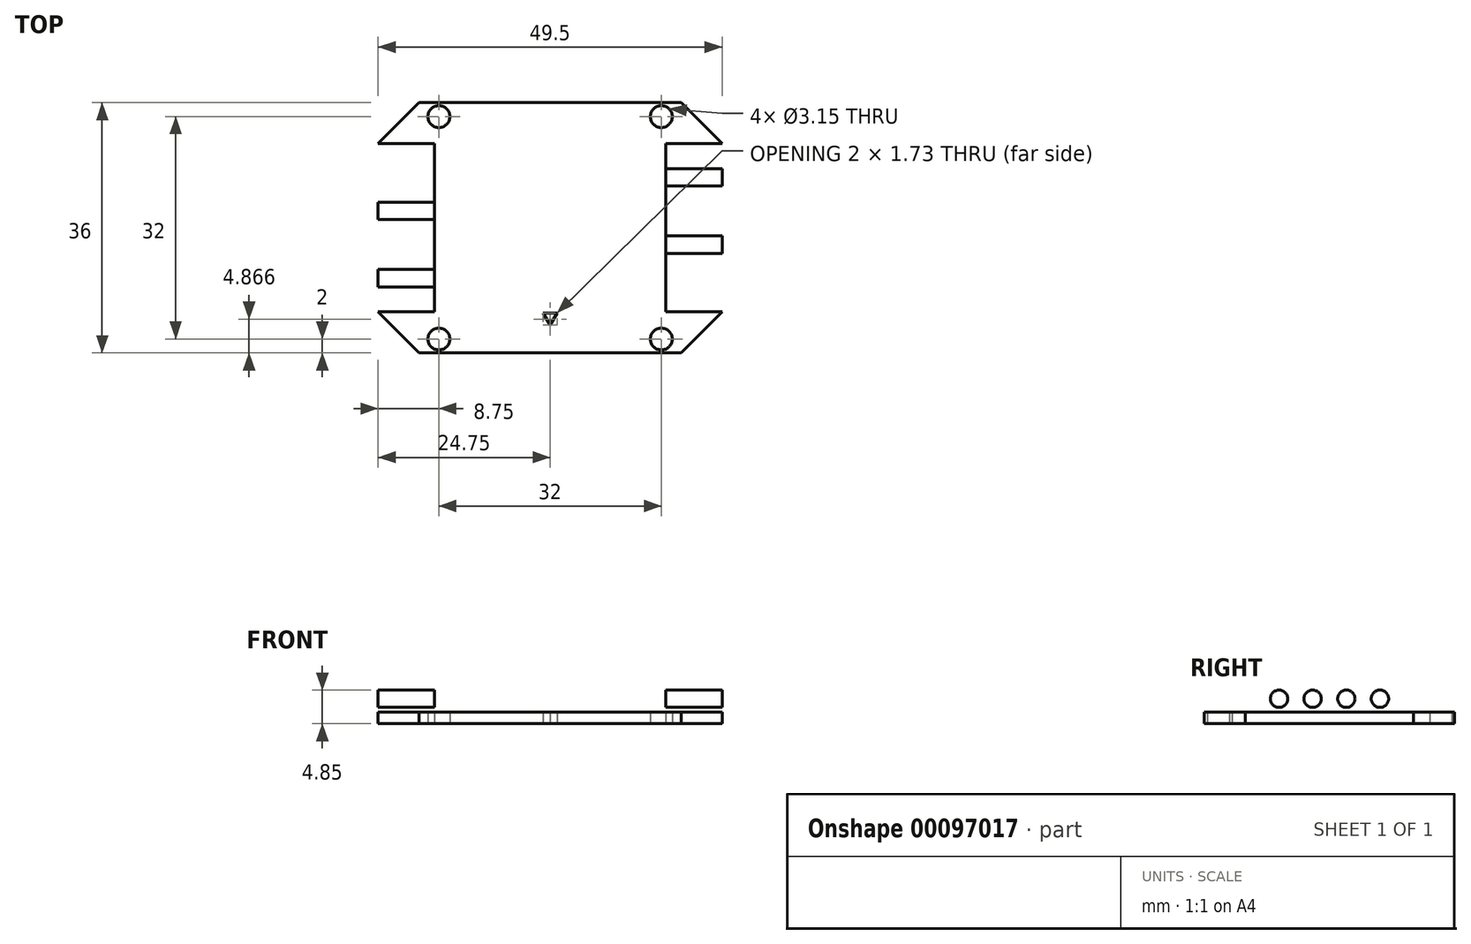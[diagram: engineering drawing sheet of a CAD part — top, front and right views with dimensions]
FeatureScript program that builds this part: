
annotation { "Feature Type Name" : "Feature", "Feature Type Description" : "" }
export const myFeature = defineFeature(function(context is Context, id is Id, definition is map)
    precondition{}
    {
        {
            var Q0;
            Q0=qCreatedBy(makeId("Top.planeOp"),FACE);
            var sketch = newSketch(context, id + "F0", { "sketchPlane" : qUnion([Q0])});
            skPoint(sketch, "E0.middle", {"position": v(0, 0) * mm});
            skCircle(sketch, "E1", {"center": v(-16, 16) * mm, "radius": 1.57 * mm});
            skCircle(sketch, "E2", {"center": v(16, 16) * mm, "radius": 1.57 * mm});
            skCircle(sketch, "E3", {"center": v(-16, -16) * mm, "radius": 1.57 * mm});
            skCircle(sketch, "E4", {"center": v(16, -16) * mm, "radius": 1.57 * mm});
            skLineSegment(sketch, "E5.bottom", {"start": v(-18.85, 18) * mm, "end": v(18.85, 18) * mm});
            skLineSegment(sketch, "E5.top", {"start": v(-18.85, -18) * mm, "end": v(18.85, -18) * mm});
            skLineSegment(sketch, "E5.left", {"start": v(-24.75, 12.1) * mm, "end": v(-24.75, -12.1) * mm});
            skLineSegment(sketch, "E5.right", {"start": v(24.75, 12.1) * mm, "end": v(24.75, -12.1) * mm});
            skLineSegment(sketch, "E6", {"start": v(24.75, 12.1) * mm, "end": v(18.85, 18) * mm});
            skLineSegment(sketch, "E7", {"start": v(24.75, -12.1) * mm, "end": v(18.85, -18) * mm});
            skLineSegment(sketch, "E8", {"start": v(-18.85, -18) * mm, "end": v(-24.75, -12.1) * mm});
            skLineSegment(sketch, "E9", {"start": v(-18.85, 18) * mm, "end": v(-24.75, 12.1) * mm});
            skLineSegment(sketch, "E10", {"start": v(0, -14) * mm, "end": v(1, -12.27) * mm});
            skLineSegment(sketch, "E11", {"start": v(1, -12.27) * mm, "end": v(-1, -12.27) * mm});
            skLineSegment(sketch, "E12", {"start": v(-1, -12.27) * mm, "end": v(0, -14) * mm});
            skLineSegment(sketch, "E13", {"start": v(-16, -16) * mm, "end": v(-16, -18) * mm});
            skLineSegment(sketch, "E14", {"start": v(16, -16) * mm, "end": v(16, -18) * mm});
            skLineSegment(sketch, "E15", {"start": v(-16, 16) * mm, "end": v(-16, 18) * mm});
            skLineSegment(sketch, "E16", {"start": v(16, 16) * mm, "end": v(16, 18) * mm});
            skLineSegment(sketch, "E17", {"start": v(-16, 16) * mm, "end": v(-20.85, 16) * mm});
            skLineSegment(sketch, "E18", {"start": v(16, 16) * mm, "end": v(20.85, 16) * mm});
            skLineSegment(sketch, "E19", {"start": v(16, -16) * mm, "end": v(20.85, -16) * mm});
            skLineSegment(sketch, "E20", {"start": v(-16, -16) * mm, "end": v(-20.85, -16) * mm});
            skSolve(sketch);
        }
        {
            var Q0;
            Q0=makeQuery(id+"F0.imprint","IMPRINT",FACE,{"disambiguationData":[TD([[makeQuery(id+"F0.imprint","IMPRINT",EDGE,{"derivedFrom":sQuery(id+"F0.wireOp",EDGE,"E1")}),-1.0]])]});
            var Q1;
            {var subQ30=sQuery(id+"F0.wireOp",EDGE,"E5.left");Q1=makeQuery(id+"F0.imprint","IMPRINT",FACE,{"disambiguationData":[TD([[makeQuery(id+"F0.imprint","IMPRINT",EDGE,{"derivedFrom":subQ30}),1.0]])]});}
            var Q2;
            {var subQ0=sQuery(id+"F0.wireOp",EDGE,"E16");var subQ3=sQuery(id+"F0.wireOp",EDGE,"E2");var subQ4=makeQuery(id+"F0.imprint","INTERSECT",VERTEX,{"derivedFrom":[subQ3,subQ0]});Q2=makeQuery(id+"F0.imprint","IMPRINT",FACE,{"disambiguationData":[TD([[makeQuery(id+"F0.imprint","IMPRINT",EDGE,{"disambiguationData":[TD([[subQ4,1.0]])],"derivedFrom":subQ3}),-1.0]])]});}
            var Q3;
            {var subQ0=sQuery(id+"F0.wireOp",EDGE,"E14");var subQ3=sQuery(id+"F0.wireOp",EDGE,"E4");var subQ4=makeQuery(id+"F0.imprint","INTERSECT",VERTEX,{"derivedFrom":[subQ3,subQ0]});Q3=makeQuery(id+"F0.imprint","IMPRINT",FACE,{"disambiguationData":[TD([[makeQuery(id+"F0.imprint","IMPRINT",EDGE,{"disambiguationData":[TD([[subQ4,-1.0]])],"derivedFrom":subQ3}),-1.0]])]});}
            var Q4;
            {var subQ0=sQuery(id+"F0.wireOp",EDGE,"E13");var subQ3=sQuery(id+"F0.wireOp",EDGE,"E3");var subQ4=makeQuery(id+"F0.imprint","INTERSECT",VERTEX,{"derivedFrom":[subQ3,subQ0]});Q4=makeQuery(id+"F0.imprint","IMPRINT",FACE,{"disambiguationData":[TD([[makeQuery(id+"F0.imprint","IMPRINT",EDGE,{"disambiguationData":[TD([[subQ4,1.0]])],"derivedFrom":subQ3}),-1.0]])]});}
            extrude(context, id + "F1", {"entities" : qUnion([Q0, Q1, Q2, Q3, Q4]), "depth" : 1.7 * mm});
        }
        {
            var Q0;
            Q0=makeQuery(id+"F1.opExtrude","CAP_FACE",FACE,{"disambiguationData":[OSD([sQuery(id+"F0.wireOp",EDGE,"E1"),sQuery(id+"F0.wireOp",EDGE,"E2"),sQuery(id+"F0.wireOp",EDGE,"E3"),sQuery(id+"F0.wireOp",EDGE,"E4"),sQuery(id+"F0.wireOp",EDGE,"E5.bottom"),sQuery(id+"F0.wireOp",EDGE,"E5.top"),sQuery(id+"F0.wireOp",EDGE,"E5.left"),sQuery(id+"F0.wireOp",EDGE,"E5.right"),sQuery(id+"F0.wireOp",EDGE,"E6"),sQuery(id+"F0.wireOp",EDGE,"E7"),sQuery(id+"F0.wireOp",EDGE,"E8"),sQuery(id+"F0.wireOp",EDGE,"E9")])],"isStart":false});
            var sketch = newSketch(context, id + "F2", { "sketchPlane" : qUnion([Q0])});
            skLineSegment(sketch, "E21.bottom", {"start": v(-24.75, 12.1) * mm, "end": v(-16.65, 12.1) * mm});
            skLineSegment(sketch, "E21.top", {"start": v(-24.75, -12.1) * mm, "end": v(-16.65, -12.1) * mm});
            skLineSegment(sketch, "E21.left", {"start": v(-24.75, 12.1) * mm, "end": v(-24.75, -12.1) * mm});
            skLineSegment(sketch, "E21.right", {"start": v(-16.65, 12.1) * mm, "end": v(-16.65, -12.1) * mm});
            skLineSegment(sketch, "E22.bottom", {"start": v(24.75, 12.1) * mm, "end": v(16.65, 12.1) * mm});
            skLineSegment(sketch, "E22.top", {"start": v(24.75, -12.1) * mm, "end": v(16.65, -12.1) * mm});
            skLineSegment(sketch, "E22.left", {"start": v(24.75, 12.1) * mm, "end": v(24.75, -12.1) * mm});
            skLineSegment(sketch, "E22.right", {"start": v(16.65, 12.1) * mm, "end": v(16.65, -12.1) * mm});
            skSolve(sketch);
        }
        {
            var Q0;
            Q0=makeQuery(id+"F2.imprint","IMPRINT",FACE,{"disambiguationData":[TD([[makeQuery(id+"F2.imprint","IMPRINT",EDGE,{"derivedFrom":sQuery(id+"F2.wireOp",EDGE,"E21.bottom")}),-1.0]])]});
            var Q1;
            Q1=makeQuery(id+"F2.imprint","IMPRINT",FACE,{"disambiguationData":[TD([[makeQuery(id+"F2.imprint","IMPRINT",EDGE,{"derivedFrom":sQuery(id+"F2.wireOp",EDGE,"E22.bottom")}),1.0]])]});
            extrude(context, id + "F3", {"entities" : qUnion([Q0, Q1]), "operationType" : NewBodyOperationType.ADD, "depth" : 5.5 * mm});
        }
        {
            var Q0;
            Q0=makeQuery(id+"F3.boolean.opBoolean","MERGE",FACE,{"derivedFrom":[makeQuery(id+"F1.opExtrude","SWEPT_FACE",FACE,{"disambiguationData":[OSD([sQuery(id+"F0.wireOp",EDGE,"E5.left")])]}),makeQuery(id+"F3.opExtrude","SWEPT_FACE",FACE,{"disambiguationData":[OSD([sQuery(id+"F2.wireOp",EDGE,"E21.left")])]})]});
            var sketch = newSketch(context, id + "F4", { "sketchPlane" : qUnion([Q0])});
            skPoint(sketch, "E23", {"position": v(-12.1, 3.6) * mm});
            skPoint(sketch, "E24", {"position": v(12.1, 3.6) * mm});
            skLineSegment(sketch, "E25", {"start": v(-12.1, 3.6) * mm, "end": v(12.1, 3.6) * mm});
            skPoint(sketch, "E26", {"position": v(-7.26, 3.6) * mm});
            skPoint(sketch, "E27", {"position": v(-2.42, 3.6) * mm});
            skPoint(sketch, "E28", {"position": v(2.42, 3.6) * mm});
            skPoint(sketch, "E29", {"position": v(12.08, 3.6) * mm});
            skPoint(sketch, "E30", {"position": v(7.26, 3.6) * mm});
            skCircle(sketch, "E31", {"center": v(-7.26, 3.6) * mm, "radius": 1.25 * mm});
            skCircle(sketch, "E32", {"center": v(-2.42, 3.6) * mm, "radius": 1.25 * mm});
            skCircle(sketch, "E33", {"center": v(2.42, 3.6) * mm, "radius": 1.25 * mm});
            skCircle(sketch, "E34", {"center": v(7.26, 3.6) * mm, "radius": 1.25 * mm});
            skSolve(sketch);
        }
        {
            var Q0;
            Q0=makeQuery(id+"F3.boolean.opBoolean","MERGE",FACE,{"derivedFrom":[makeQuery(id+"F1.opExtrude","SWEPT_FACE",FACE,{"disambiguationData":[OSD([sQuery(id+"F0.wireOp",EDGE,"E5.right")])]}),makeQuery(id+"F3.opExtrude","SWEPT_FACE",FACE,{"disambiguationData":[OSD([sQuery(id+"F2.wireOp",EDGE,"E22.left")])]})]});
            var sketch = newSketch(context, id + "F5", { "sketchPlane" : qUnion([Q0])});
            skPoint(sketch, "E35", {"position": v(-12.1, 3.6) * mm});
            skPoint(sketch, "E36", {"position": v(12.1, 3.6) * mm});
            skLineSegment(sketch, "E37", {"start": v(-12.1, 3.6) * mm, "end": v(12.1, 3.6) * mm});
            skPoint(sketch, "E38", {"position": v(-7.26, 3.6) * mm});
            skPoint(sketch, "E39", {"position": v(-2.42, 3.6) * mm});
            skPoint(sketch, "E40", {"position": v(2.42, 3.6) * mm});
            skPoint(sketch, "E41", {"position": v(7.26, 3.6) * mm});
            skCircle(sketch, "E42", {"center": v(-7.26, 3.6) * mm, "radius": 1.25 * mm});
            skCircle(sketch, "E43", {"center": v(-2.42, 3.6) * mm, "radius": 1.25 * mm});
            skCircle(sketch, "E44", {"center": v(2.42, 3.6) * mm, "radius": 1.25 * mm});
            skCircle(sketch, "E45", {"center": v(7.26, 3.6) * mm, "radius": 1.25 * mm});
            skSolve(sketch);
        }
        {
            var Q0;
            {var subQ0=sQuery(id+"F5.wireOp",EDGE,"E45");var subQ1=sQuery(id+"F5.wireOp",EDGE,"E37");var subQ2=makeQuery(id+"F5.imprint","INTERSECT",VERTEX,{"disambiguationData":[OD(0.0)],"derivedFrom":[subQ1,subQ0]});Q0=makeQuery(id+"F5.imprint","IMPRINT",FACE,{"disambiguationData":[TD([[makeQuery(id+"F5.imprint","IMPRINT",EDGE,{"disambiguationData":[TD([[subQ2,-1.0]])],"derivedFrom":subQ1}),1.0]])]});}
            var Q1;
            {var subQ0=sQuery(id+"F5.wireOp",EDGE,"E45");var subQ1=sQuery(id+"F5.wireOp",EDGE,"E37");var subQ2=makeQuery(id+"F5.imprint","INTERSECT",VERTEX,{"disambiguationData":[OD(0.0)],"derivedFrom":[subQ1,subQ0]});Q1=makeQuery(id+"F5.imprint","IMPRINT",FACE,{"disambiguationData":[TD([[makeQuery(id+"F5.imprint","IMPRINT",EDGE,{"disambiguationData":[TD([[subQ2,-1.0]])],"derivedFrom":subQ1}),-1.0]])]});}
            var Q2;
            {var subQ0=sQuery(id+"F5.wireOp",EDGE,"E44");var subQ1=sQuery(id+"F5.wireOp",EDGE,"E37");var subQ2=makeQuery(id+"F5.imprint","INTERSECT",VERTEX,{"disambiguationData":[OD(0.0)],"derivedFrom":[subQ1,subQ0]});Q2=makeQuery(id+"F5.imprint","IMPRINT",FACE,{"disambiguationData":[TD([[makeQuery(id+"F5.imprint","IMPRINT",EDGE,{"disambiguationData":[TD([[subQ2,-1.0]])],"derivedFrom":subQ1}),-1.0]])]});}
            var Q3;
            {var subQ0=sQuery(id+"F5.wireOp",EDGE,"E44");var subQ1=sQuery(id+"F5.wireOp",EDGE,"E37");var subQ2=makeQuery(id+"F5.imprint","INTERSECT",VERTEX,{"disambiguationData":[OD(0.0)],"derivedFrom":[subQ1,subQ0]});Q3=makeQuery(id+"F5.imprint","IMPRINT",FACE,{"disambiguationData":[TD([[makeQuery(id+"F5.imprint","IMPRINT",EDGE,{"disambiguationData":[TD([[subQ2,-1.0]])],"derivedFrom":subQ1}),1.0]])]});}
            var Q4;
            {var subQ0=sQuery(id+"F5.wireOp",EDGE,"E43");var subQ1=sQuery(id+"F5.wireOp",EDGE,"E37");var subQ2=makeQuery(id+"F5.imprint","INTERSECT",VERTEX,{"disambiguationData":[OD(0.0)],"derivedFrom":[subQ1,subQ0]});Q4=makeQuery(id+"F5.imprint","IMPRINT",FACE,{"disambiguationData":[TD([[makeQuery(id+"F5.imprint","IMPRINT",EDGE,{"disambiguationData":[TD([[subQ2,-1.0]])],"derivedFrom":subQ1}),-1.0]])]});}
            var Q5;
            {var subQ0=sQuery(id+"F5.wireOp",EDGE,"E43");var subQ1=sQuery(id+"F5.wireOp",EDGE,"E37");var subQ2=makeQuery(id+"F5.imprint","INTERSECT",VERTEX,{"disambiguationData":[OD(0.0)],"derivedFrom":[subQ1,subQ0]});Q5=makeQuery(id+"F5.imprint","IMPRINT",FACE,{"disambiguationData":[TD([[makeQuery(id+"F5.imprint","IMPRINT",EDGE,{"disambiguationData":[TD([[subQ2,-1.0]])],"derivedFrom":subQ1}),1.0]])]});}
            var Q6;
            {var subQ0=sQuery(id+"F5.wireOp",EDGE,"E42");var subQ1=sQuery(id+"F5.wireOp",EDGE,"E37");var subQ2=makeQuery(id+"F5.imprint","INTERSECT",VERTEX,{"disambiguationData":[OD(0.0)],"derivedFrom":[subQ1,subQ0]});Q6=makeQuery(id+"F5.imprint","IMPRINT",FACE,{"disambiguationData":[TD([[makeQuery(id+"F5.imprint","IMPRINT",EDGE,{"disambiguationData":[TD([[subQ2,-1.0]])],"derivedFrom":subQ1}),-1.0]])]});}
            var Q7;
            {var subQ0=sQuery(id+"F5.wireOp",EDGE,"E42");var subQ1=sQuery(id+"F5.wireOp",EDGE,"E37");var subQ2=makeQuery(id+"F5.imprint","INTERSECT",VERTEX,{"disambiguationData":[OD(0.0)],"derivedFrom":[subQ1,subQ0]});Q7=makeQuery(id+"F5.imprint","IMPRINT",FACE,{"disambiguationData":[TD([[makeQuery(id+"F5.imprint","IMPRINT",EDGE,{"disambiguationData":[TD([[subQ2,-1.0]])],"derivedFrom":subQ1}),1.0]])]});}
            extrude(context, id + "F6", {"entities" : qUnion([Q0, Q1, Q2, Q3, Q4, Q5, Q6, Q7]), "operationType" : NewBodyOperationType.REMOVE, "oppositeDirection" : true, "depth" : 8.1 * mm});
        }
        {
            var Q0;
            {var subQ0=sQuery(id+"F4.wireOp",EDGE,"E34");var subQ1=sQuery(id+"F4.wireOp",EDGE,"E25");var subQ2=makeQuery(id+"F4.imprint","INTERSECT",VERTEX,{"disambiguationData":[OD(0.0)],"derivedFrom":[subQ1,subQ0]});Q0=makeQuery(id+"F4.imprint","IMPRINT",FACE,{"disambiguationData":[TD([[makeQuery(id+"F4.imprint","IMPRINT",EDGE,{"disambiguationData":[TD([[subQ2,-1.0]])],"derivedFrom":subQ1}),1.0]])]});}
            var Q1;
            {var subQ0=sQuery(id+"F4.wireOp",EDGE,"E34");var subQ1=sQuery(id+"F4.wireOp",EDGE,"E25");var subQ2=makeQuery(id+"F4.imprint","INTERSECT",VERTEX,{"disambiguationData":[OD(0.0)],"derivedFrom":[subQ1,subQ0]});Q1=makeQuery(id+"F4.imprint","IMPRINT",FACE,{"disambiguationData":[TD([[makeQuery(id+"F4.imprint","IMPRINT",EDGE,{"disambiguationData":[TD([[subQ2,-1.0]])],"derivedFrom":subQ1}),-1.0]])]});}
            var Q2;
            {var subQ0=sQuery(id+"F4.wireOp",EDGE,"E33");var subQ1=sQuery(id+"F4.wireOp",EDGE,"E25");var subQ2=makeQuery(id+"F4.imprint","INTERSECT",VERTEX,{"disambiguationData":[OD(0.0)],"derivedFrom":[subQ1,subQ0]});Q2=makeQuery(id+"F4.imprint","IMPRINT",FACE,{"disambiguationData":[TD([[makeQuery(id+"F4.imprint","IMPRINT",EDGE,{"disambiguationData":[TD([[subQ2,-1.0]])],"derivedFrom":subQ1}),1.0]])]});}
            var Q3;
            {var subQ0=sQuery(id+"F4.wireOp",EDGE,"E33");var subQ1=sQuery(id+"F4.wireOp",EDGE,"E25");var subQ2=makeQuery(id+"F4.imprint","INTERSECT",VERTEX,{"disambiguationData":[OD(0.0)],"derivedFrom":[subQ1,subQ0]});Q3=makeQuery(id+"F4.imprint","IMPRINT",FACE,{"disambiguationData":[TD([[makeQuery(id+"F4.imprint","IMPRINT",EDGE,{"disambiguationData":[TD([[subQ2,-1.0]])],"derivedFrom":subQ1}),-1.0]])]});}
            var Q4;
            {var subQ0=sQuery(id+"F4.wireOp",EDGE,"E32");var subQ1=sQuery(id+"F4.wireOp",EDGE,"E25");var subQ2=makeQuery(id+"F4.imprint","INTERSECT",VERTEX,{"disambiguationData":[OD(0.0)],"derivedFrom":[subQ1,subQ0]});Q4=makeQuery(id+"F4.imprint","IMPRINT",FACE,{"disambiguationData":[TD([[makeQuery(id+"F4.imprint","IMPRINT",EDGE,{"disambiguationData":[TD([[subQ2,-1.0]])],"derivedFrom":subQ1}),1.0]])]});}
            var Q5;
            {var subQ0=sQuery(id+"F4.wireOp",EDGE,"E32");var subQ1=sQuery(id+"F4.wireOp",EDGE,"E25");var subQ2=makeQuery(id+"F4.imprint","INTERSECT",VERTEX,{"disambiguationData":[OD(0.0)],"derivedFrom":[subQ1,subQ0]});Q5=makeQuery(id+"F4.imprint","IMPRINT",FACE,{"disambiguationData":[TD([[makeQuery(id+"F4.imprint","IMPRINT",EDGE,{"disambiguationData":[TD([[subQ2,-1.0]])],"derivedFrom":subQ1}),-1.0]])]});}
            var Q6;
            {var subQ0=sQuery(id+"F4.wireOp",EDGE,"E31");var subQ1=sQuery(id+"F4.wireOp",EDGE,"E25");var subQ2=makeQuery(id+"F4.imprint","INTERSECT",VERTEX,{"disambiguationData":[OD(0.0)],"derivedFrom":[subQ1,subQ0]});Q6=makeQuery(id+"F4.imprint","IMPRINT",FACE,{"disambiguationData":[TD([[makeQuery(id+"F4.imprint","IMPRINT",EDGE,{"disambiguationData":[TD([[subQ2,-1.0]])],"derivedFrom":subQ1}),1.0]])]});}
            var Q7;
            {var subQ0=sQuery(id+"F4.wireOp",EDGE,"E31");var subQ1=sQuery(id+"F4.wireOp",EDGE,"E25");var subQ2=makeQuery(id+"F4.imprint","INTERSECT",VERTEX,{"disambiguationData":[OD(0.0)],"derivedFrom":[subQ1,subQ0]});Q7=makeQuery(id+"F4.imprint","IMPRINT",FACE,{"disambiguationData":[TD([[makeQuery(id+"F4.imprint","IMPRINT",EDGE,{"disambiguationData":[TD([[subQ2,-1.0]])],"derivedFrom":subQ1}),-1.0]])]});}
            extrude(context, id + "F7", {"entities" : qUnion([Q0, Q1, Q2, Q3, Q4, Q5, Q6, Q7]), "operationType" : NewBodyOperationType.REMOVE, "oppositeDirection" : true, "depth" : 8.1 * mm});
        }
    });
